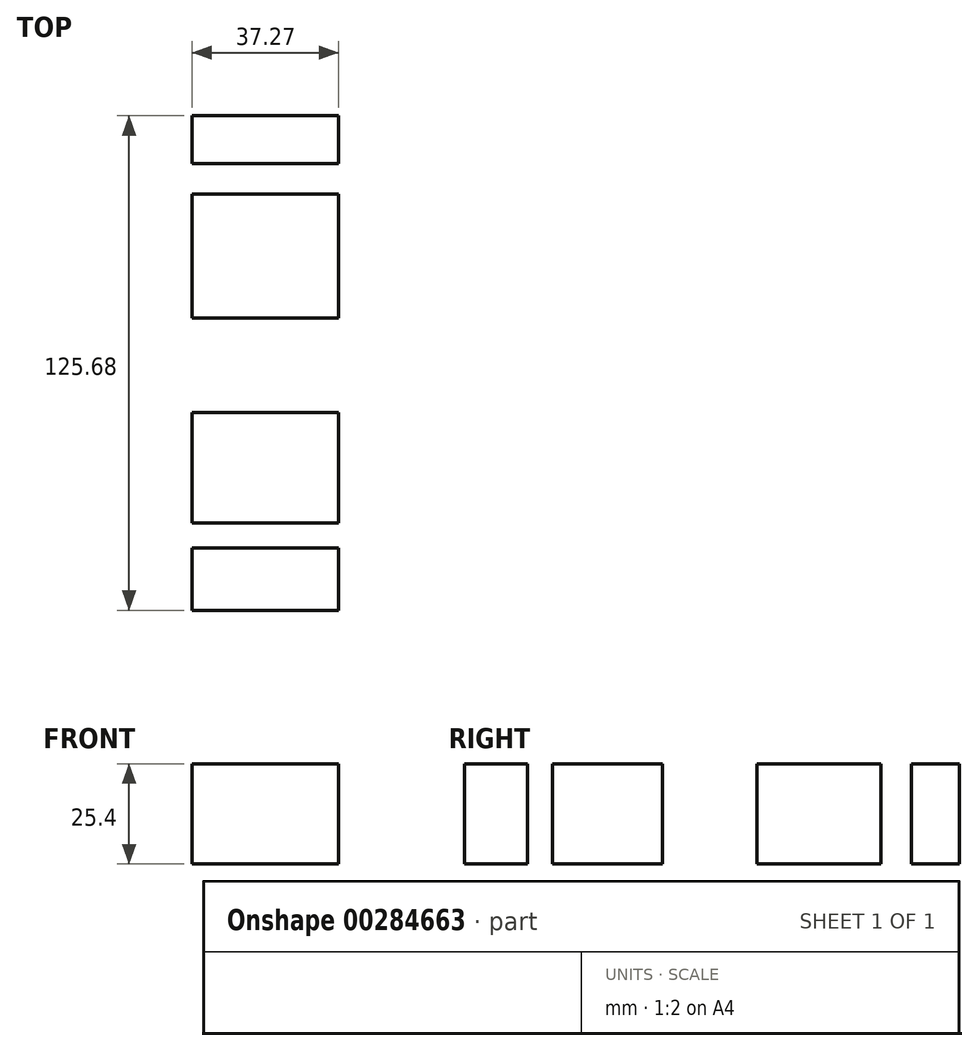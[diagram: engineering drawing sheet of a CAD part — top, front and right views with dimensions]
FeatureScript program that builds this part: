
annotation { "Feature Type Name" : "Feature", "Feature Type Description" : "" }
export const myFeature = defineFeature(function(context is Context, id is Id, definition is map)
    precondition{}
    {
        {
            var Q0;
            Q0=qCreatedBy(makeId("Top.planeOp"),FACE);
            var sketch = newSketch(context, id + "F0", { "sketchPlane" : qUnion([Q0])});
            skLineSegment(sketch, "E0.bottom", {"start": v(-43.05, 58.94) * mm, "end": v(-5.78, 58.94) * mm});
            skLineSegment(sketch, "E0.top", {"start": v(-43.05, -66.74) * mm, "end": v(-5.78, -66.74) * mm});
            skLineSegment(sketch, "E0.left", {"start": v(-43.05, 58.94) * mm, "end": v(-43.05, -66.74) * mm});
            skLineSegment(sketch, "E0.right", {"start": v(-5.78, 58.94) * mm, "end": v(-5.78, -66.74) * mm});
            skLineSegment(sketch, "E1.bottom", {"start": v(-43.05, 46.8) * mm, "end": v(-5.78, 46.8) * mm});
            skLineSegment(sketch, "E1.top", {"start": v(-43.05, 39) * mm, "end": v(-5.78, 39) * mm});
            skLineSegment(sketch, "E1.left", {"start": v(-43.05, 46.8) * mm, "end": v(-43.05, 39) * mm});
            skLineSegment(sketch, "E1.right", {"start": v(-5.78, 46.8) * mm, "end": v(-5.78, 39) * mm});
            skLineSegment(sketch, "E2.bottom", {"start": v(-43.05, 7.51) * mm, "end": v(-5.78, 7.51) * mm});
            skLineSegment(sketch, "E2.top", {"start": v(-43.05, -16.47) * mm, "end": v(-5.78, -16.47) * mm});
            skLineSegment(sketch, "E2.left", {"start": v(-43.05, 7.51) * mm, "end": v(-43.05, -16.47) * mm});
            skLineSegment(sketch, "E2.right", {"start": v(-5.78, 7.51) * mm, "end": v(-5.78, -16.47) * mm});
            skLineSegment(sketch, "E3.bottom", {"start": v(-43.05, -44.5) * mm, "end": v(-5.78, -44.5) * mm});
            skLineSegment(sketch, "E3.top", {"start": v(-43.05, -50.85) * mm, "end": v(-5.78, -50.85) * mm});
            skLineSegment(sketch, "E3.left", {"start": v(-43.05, -44.5) * mm, "end": v(-43.05, -50.85) * mm});
            skLineSegment(sketch, "E3.right", {"start": v(-5.78, -44.5) * mm, "end": v(-5.78, -50.85) * mm});
            skSolve(sketch);
        }
        {
            var Q0;
            {var subQ0=sQuery(id+"F0.wireOp",EDGE,"E0.bottom");Q0=makeQuery(id+"F0.imprint","IMPRINT",FACE,{"disambiguationData":[TD([[makeQuery(id+"F0.imprint","IMPRINT",EDGE,{"derivedFrom":subQ0}),-1.0]])]});}
            var Q1;
            {var subQ0=sQuery(id+"F0.wireOp",EDGE,"E0.top");Q1=makeQuery(id+"F0.imprint","IMPRINT",FACE,{"disambiguationData":[TD([[makeQuery(id+"F0.imprint","IMPRINT",EDGE,{"derivedFrom":subQ0}),1.0]])]});}
            var Q2;
            {var subQ0=sQuery(id+"F0.wireOp",EDGE,"E1.top");Q2=makeQuery(id+"F0.imprint","IMPRINT",FACE,{"disambiguationData":[TD([[makeQuery(id+"F0.imprint","IMPRINT",EDGE,{"derivedFrom":subQ0}),-1.0]])]});}
            var Q3;
            {var subQ0=sQuery(id+"F0.wireOp",EDGE,"E2.top");Q3=makeQuery(id+"F0.imprint","IMPRINT",FACE,{"disambiguationData":[TD([[makeQuery(id+"F0.imprint","IMPRINT",EDGE,{"derivedFrom":subQ0}),-1.0]])]});}
            extrude(context, id + "F1", {"entities" : qUnion([Q0, Q1, Q2, Q3]), "depth" : 25.4 * mm});
        }
    });
